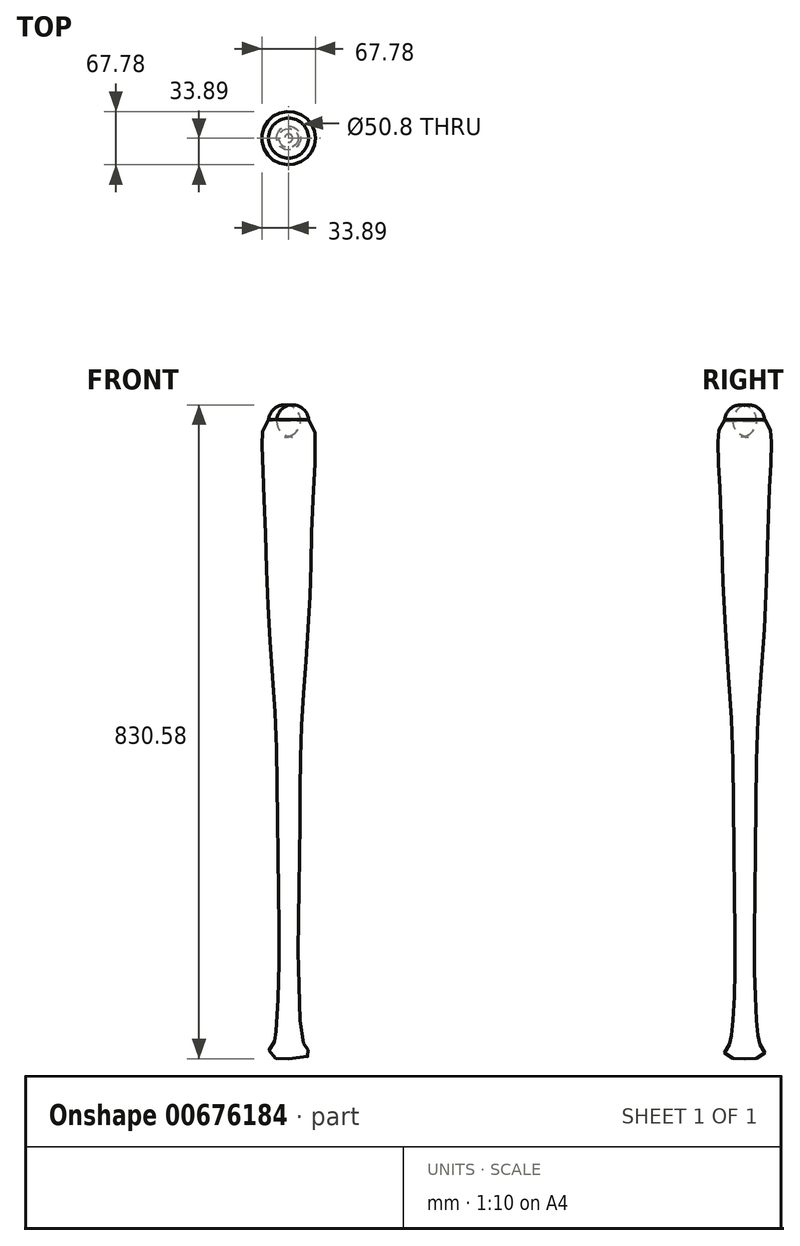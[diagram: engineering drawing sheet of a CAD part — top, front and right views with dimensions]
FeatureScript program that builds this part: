
annotation { "Feature Type Name" : "Feature", "Feature Type Description" : "" }
export const myFeature = defineFeature(function(context is Context, id is Id, definition is map)
    precondition{}
    {
        {
            var Q0;
            Q0=qCreatedBy(makeId("Front.planeOp"),FACE);
            var sketch = newSketch(context, id + "F0", { "sketchPlane" : qUnion([Q0])});
            skFitSpline(sketch, "E0", {"points": [v(0, 0) * mm, v(24.95, 4.27) * mm, v(25.4, 8.88) * mm, v(22.73, 14.12) * mm, v(19.05, 19.05) * mm, v(12.7, 101.6) * mm, v(12.7, 203.2) * mm, v(14.29, 304.8) * mm, v(15.88, 406.4) * mm, v(22.23, 508) * mm, v(27.79, 609.6) * mm, v(30.96, 711.2) * mm, v(31.75, 804.42) * mm, v(0, 812.8) * mm], "startDerivative": vector(1235.4, 0) * mm, "endDerivative": vector(-1213.33, -5.02) * mm});
            skLineSegment(sketch, "E1", {"start": v(0, 0) * mm, "end": v(0, 812.8) * mm, "construction": true});
            skLineSegment(sketch, "E2", {"start": v(0, 812.8) * mm, "end": v(0, 0) * mm});
            skSolve(sketch);
        }
        {
            var Q0;
            Q0=qSketchRegion(id+"F0",true);
            var Q1;
            Q1=sQuery(id+"F0.wireOp",EDGE,"E2");
            revolve(context, id + "F1", {"entities" : qUnion([Q0]), "axis" : qUnion([Q1]), "revolveType" : RevolveType.FULL});
        }
        {
            var Q0;
            Q0=qCreatedBy(makeId("Top.planeOp"),FACE);
            cPlane(context, id + "F2", {"entities" : qUnion([Q0]), "cplaneType" : CPlaneType.OFFSET, "offset" : 815.34 * mm, "width" : 152.4 * mm, "height" : 152.4 * mm});
        }
        {
            var Q0;
            Q0=qCreatedBy(id+"F2.planeOp",FACE);
            var sketch = newSketch(context, id + "F3", { "sketchPlane" : qUnion([Q0])});
            skCircle(sketch, "E3", {"center": v(0, 0) * mm, "radius": 25.4 * mm});
            skSolve(sketch);
        }
        {
            var Q0;
            Q0=qSketchRegion(id+"F3",true);
            extrude(context, id + "F4", {"entities" : qUnion([Q0]), "operationType" : NewBodyOperationType.REMOVE, "oppositeDirection" : true, "depth" : 25.4 * mm});
        }
        {
            var Q0;
            Q0=makeQuery(id+"F4.boolean.opBoolean","COPY",EDGE,{"derivedFrom":makeQuery(id+"F4.opExtrude","CAP_EDGE",EDGE,{"disambiguationData":[OSD([sQuery(id+"F3.wireOp",EDGE,"E3")])],"isStart":false})});
            fillet(context, id + "F5", {"entities" : qUnion([Q0]), "radius" : 20.32 * mm, "tangentPropagation" : true, "allowEdgeOverflow" : false});
        }
        {
            var Q0;
            Q0=makeQuery(id+"F1.opRevolve","SWEPT_FACE",FACE,{"disambiguationData":[OSD([sQuery(id+"F0.wireOp",EDGE,"E0")])]});
            cPlane(context, id + "F6", {"entities" : qUnion([Q0]), "cplaneType" : CPlaneType.LINE_ANGLE, "offset" : 25.4 * mm, "angle" : 360 * degree, "width" : 152.4 * mm, "height" : 152.4 * mm});
        }
        {
            var Q0;
            Q0=qCreatedBy(id+"F6.planeOp",FACE);
            var sketch = newSketch(context, id + "F7", { "sketchPlane" : qUnion([Q0])});
            skLineSegment(sketch, "E4.bottom", {"start": v(-25.58, 727.73) * mm, "end": v(25.58, 727.73) * mm});
            skLineSegment(sketch, "E4.top", {"start": v(-25.58, 651.94) * mm, "end": v(25.58, 651.94) * mm});
            skLineSegment(sketch, "E4.left", {"start": v(-25.58, 727.73) * mm, "end": v(-25.58, 651.94) * mm});
            skLineSegment(sketch, "E4.right", {"start": v(25.58, 727.73) * mm, "end": v(25.58, 651.94) * mm});
            skPoint(sketch, "E4.middle", {"position": v(0, 689.83) * mm});
            skSolve(sketch);
        }
        {
            var Q0;
            Q0 = qSketchRegion(id + "F7", true);
            extrude(context, id + "F8", {"entities" : qUnion([Q0]), "operationType" : NewBodyOperationType.ADD, "depth" : 12.7 * mm, "offsetDistance" : 25.4 * mm});
        }
    });
